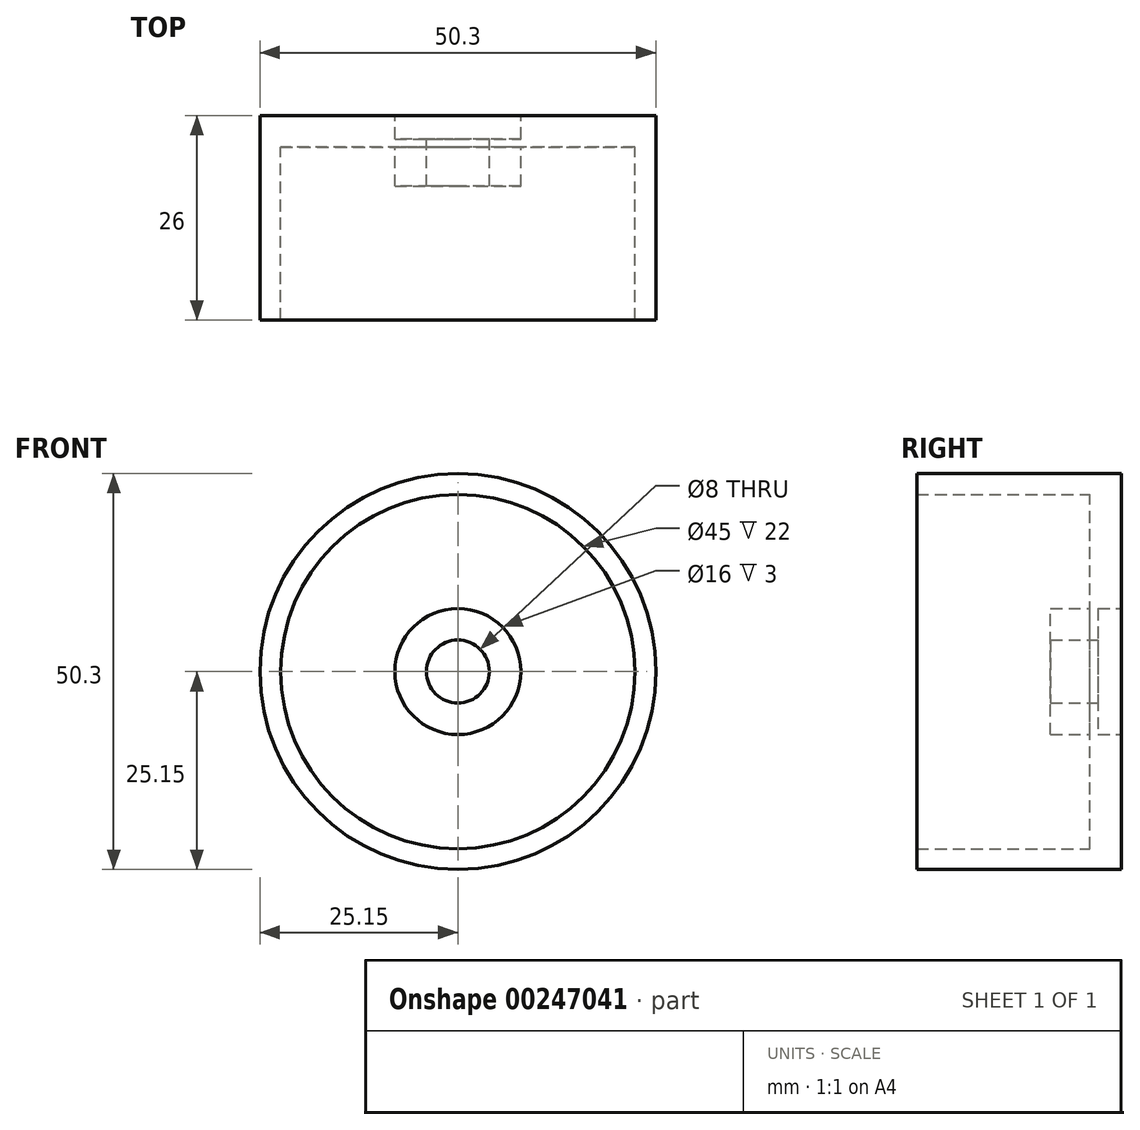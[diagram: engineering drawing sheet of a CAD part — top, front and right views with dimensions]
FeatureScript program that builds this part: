
annotation { "Feature Type Name" : "Feature", "Feature Type Description" : "" }
export const myFeature = defineFeature(function(context is Context, id is Id, definition is map)
    precondition{}
    {
        {
            var Q0;
            Q0=qCreatedBy(makeId("Front.planeOp"),FACE);
            var sketch = newSketch(context, id + "F0", { "sketchPlane" : qUnion([Q0])});
            skCircle(sketch, "E0", {"center": v(0, 0) * mm, "radius": 25.15 * mm});
            skSolve(sketch);
        }
        {
            var Q0;
            Q0=makeQuery(id+"F0.imprint","IMPRINT",FACE,{"disambiguationData":[TD([[makeQuery(id+"F0.imprint","IMPRINT",EDGE,{"derivedFrom":sQuery(id+"F0.wireOp",EDGE,"E0")}),1.0]])]});
            extrude(context, id + "F1", {"entities" : qUnion([Q0]), "depth" : 4 * mm});
        }
        {
            var Q0;
            Q0=makeQuery(id+"F1.opExtrude","CAP_FACE",FACE,{"disambiguationData":[OSD([sQuery(id+"F0.wireOp",EDGE,"E0")])],"isStart":false});
            var sketch = newSketch(context, id + "F2", { "sketchPlane" : qUnion([Q0])});
            skCircle(sketch, "E1", {"center": v(0, 0) * mm, "radius": 22.5 * mm});
            skSolve(sketch);
        }
        {
            var Q0;
            Q0=makeQuery(id+"F2.imprint","IMPRINT",FACE,{"disambiguationData":[TD([[makeQuery(id+"F2.imprint","IMPRINT",EDGE,{"derivedFrom":makeQuery(id+"F1.opExtrude","CAP_EDGE",EDGE,{"disambiguationData":[OSD([sQuery(id+"F0.wireOp",EDGE,"E0")])],"isStart":false})}),1.0]])]});
            extrude(context, id + "F3", {"entities" : qUnion([Q0]), "operationType" : NewBodyOperationType.ADD, "depth" : 22 * mm});
        }
        {
            var Q0;
            Q0=makeQuery(id+"F1.opExtrude","CAP_FACE",FACE,{"disambiguationData":[OSD([sQuery(id+"F0.wireOp",EDGE,"E0")])],"isStart":false});
            var sketch = newSketch(context, id + "F4", { "sketchPlane" : qUnion([Q0])});
            skCircle(sketch, "E2", {"center": v(0, 0) * mm, "radius": 8 * mm});
            skSolve(sketch);
        }
        {
            var Q0;
            Q0 = qSketchRegion(id + "F4", true);
            extrude(context, id + "F5", {"entities" : qUnion([Q0]), "operationType" : NewBodyOperationType.ADD, "depth" : 5 * mm});
        }
        {
            var Q0;
            Q0=makeQuery(id+"F1.opExtrude","CAP_FACE",FACE,{"disambiguationData":[OSD([sQuery(id+"F0.wireOp",EDGE,"E0")])],"isStart":true});
            var sketch = newSketch(context, id + "F6", { "sketchPlane" : qUnion([Q0])});
            skCircle(sketch, "E3", {"center": v(0, 0) * mm, "radius": 4 * mm});
            skSolve(sketch);
        }
        {
            var Q0;
            Q0 = qSketchRegion(id + "F6", true);
            extrude(context, id + "F7", {"entities" : qUnion([Q0]), "operationType" : NewBodyOperationType.REMOVE, "oppositeDirection" : true, "depth" : 25 * mm});
        }
        {
            var Q0;
            Q0=makeQuery(id+"F1.opExtrude","CAP_FACE",FACE,{"disambiguationData":[OSD([sQuery(id+"F0.wireOp",EDGE,"E0")])],"isStart":true});
            var sketch = newSketch(context, id + "F8", { "sketchPlane" : qUnion([Q0])});
            skCircle(sketch, "E4", {"center": v(0, 0) * mm, "radius": 8 * mm});
            skSolve(sketch);
        }
        {
            var Q0;
            Q0 = qSketchRegion(id + "F8", true);
            extrude(context, id + "F9", {"entities" : qUnion([Q0]), "operationType" : NewBodyOperationType.REMOVE, "oppositeDirection" : true, "depth" : 3 * mm});
        }
    });
